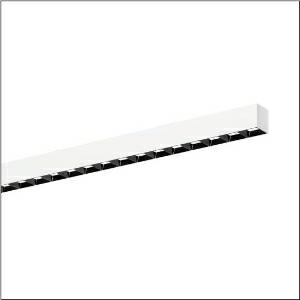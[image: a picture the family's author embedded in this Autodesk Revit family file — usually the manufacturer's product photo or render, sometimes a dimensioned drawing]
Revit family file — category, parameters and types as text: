
# Revit family: silica_r__21_51mx21tbt5w_e527
name_source: partatom
category: Lighting Fixtures
units: mm (PartAtom-declared; Revit-internal decimal feet)

## family parameters
Cut with Voids When Loaded = No
Host = Face
Light Source = No
Part Type = Normal
Room Calculation Point = No
Round Connector Dimension = Use Diameter
Shared = No

## types (1)
- --- (1 x LED, 4650 lm, 40.3 W, 6500K)
    Apparent Load = 40 VA
    CIE Flux Codes = 85 99 100 100 100
    Color Rendering = 80
    Color Temperature = 6500K
    Default Elevation = 1800 mm
    Description = Silica® 21, office luminaire, primary light control with darklight reflector, of PMMA, black, CAT 2 (L<= 3000cd/m²), light emission: direct distribution, primary light characteristic: symmetric, installation type: surface-mounted, LED, rated luminous flux: 4.650lm, luminous efficacy: 110lm/W, light colour: 8tw, colour temperature: 2700..6500K, control gear: DALI DT8, with terminal, 3+2-pole, max. 2.5mm², mains connection: 220..240V, AC, 50/60Hz, rated input power: 42.3W, luminaire housing, of aluminium, traffic white (RAL 9016), length: 1.504mm, width: 53mm, height: 53mm, protection rating (complete): IP20, insulation class (complete): insulation class I (protective earthing), certification: CE, permissible operating ambient temperature: 0..+35°C, standard: EN 50419, packaging unit: 1 piece
    Height = 53 mm
    Lamp = 1 x LED
    Lamp Light Flux = 4650 lm
    Lamp Power = 40.3 W
    Lamp count = 1
    Length = 1504 mm
    Luminous efficacy = 115 lm/W
    Manufacturer = Siteco
    ModVariant = No
    Model = 51MX21TBT5W
    Mounting Place = Ceiling
    Mounting Type = Surface mounted
    Number of Poles = 1
    OnlyDefault = Yes
    Power Factor = 1
    Product Name = Silica® 21
    Product group = office luminaire | ceiling mounted
    ProductGroupID = 303
    Protection Class = Protection class I
    Protection Degree = IP 20
    RLX_Detail_Level = 1
    RLX_Emergency_Light_Flux = 0 lm
    RLX_Emergency_Type = 0
    RLX_Emergency_Type_DB = No
    RlxData = <blob elided: 41477 chars, md5=b8afe924>
    Socket = socket
    Standby Power = 0 W
    System Light Flux = 4650 lm
    System Power = 40 W
    Type Comments = individual setting
    Type Image = l_1335873.jpg
    URL = http://relux.com
    VarID = @adj_161561
    Voltage = 0 V
    Weight = 0.00 kg
    Width = 53 mm

## geometry (parser evidence)
native form markers: Blend x4, Sweep x9
no freeform markers — native parametric forms only
